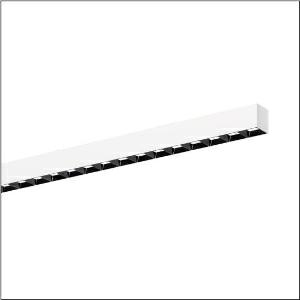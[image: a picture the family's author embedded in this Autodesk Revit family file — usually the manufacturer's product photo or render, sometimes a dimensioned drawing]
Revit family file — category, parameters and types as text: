
# Revit family: silica_r__21_51mx22tbt5w_cdcc
name_source: partatom
category: Lighting Fixtures
units: mm (PartAtom-declared; Revit-internal decimal feet)

## family parameters
Cut with Voids When Loaded = No
Host = Face
Light Source = No
Part Type = Normal
Room Calculation Point = No
Round Connector Dimension = Use Diameter
Shared = No

## types (1)
- --- (1 x LED, 4650 lm, 40.2 W, 6500K)
    Apparent Load = 40 VA
    CIE Flux Codes = 84 100 100 100 100
    Color Rendering = 80
    Color Temperature = 6500K
    Default Elevation = 1800 mm
    Description = Silica® 21, office luminaire, primary light control with darklight reflector, of PMMA, black, CAT 2 (L<= 3000cd/m²), light emission: direct distribution, primary light characteristic: symmetric, installation type: surface-mounted, LED, rated luminous flux: 4.650lm, luminous efficacy: 110lm/W, light colour: 8tw, colour temperature: 2700..6500K, control gear: ECG DALI, with terminal, 3+2-pole, max. 2.5mm², mains connection: 220..240V, AC, 50/60Hz, rated input power: 42.2W, luminaire housing, of aluminium, traffic white (RAL 9016), length: 1.504mm, width: 53mm, height: 53mm, protection rating (complete): IP20, insulation class (complete): insulation class I (protective earthing), certification: CE, permissible operating ambient temperature: 0..+35°C, standard: EN 50419, packaging unit: 1 piece
    Height = 0 mm  [stored 0 ft]
    Lamp = 1 x LED
    Lamp Light Flux = 4650 lm
    Lamp Power = 40.2 W
    Lamp count = 1
    Length = 1504 mm
    Luminous efficacy = 116 lm/W
    Manufacturer = Siteco
    ModVariant = No
    Model = 51MX22TBT5W
    Mounting Place = Ceiling
    Mounting Type = Recessed
    Number of Poles = 1
    OnlyDefault = Yes
    Power Factor = 1
    Product Name = Silica® 21
    Product group = office luminaire | ceiling recessed
    ProductGroupID = 401
    Protection Class = Protection class I
    Protection Degree = IP 20
    RLX_Detail_Level = 1
    RLX_Emergency_Light_Flux = 0 lm
    RLX_Emergency_Type = 0
    RLX_Emergency_Type_DB = No
    RlxData = <blob elided: 41349 chars, md5=5af7188b>
    Socket = socket
    Standby Power = 0 W
    System Light Flux = 4650 lm
    System Power = 40 W
    Type Comments = individual setting
    Type Image = l_1313592.jpg
    URL = http://relux.com
    VarID = @adj_089523
    Voltage = 0 V
    Weight = 0.00 kg
    Width = 53 mm

note: [stored X ft] marks values corroborated as IEEE doubles in the binary element streams (Revit-internal decimal feet)

## geometry (parser evidence)
native form markers: Blend x4, Sweep x12
no freeform markers — native parametric forms only
